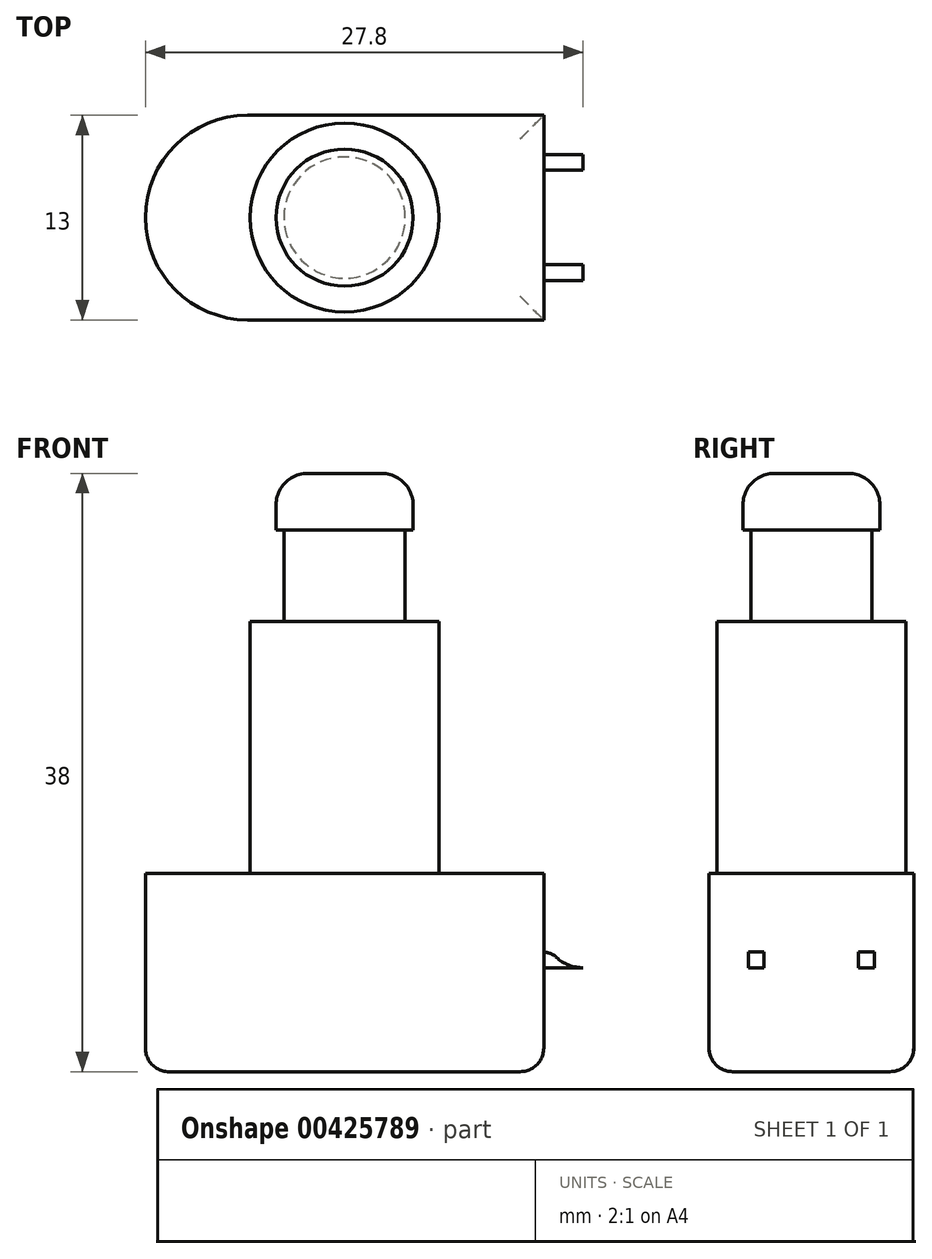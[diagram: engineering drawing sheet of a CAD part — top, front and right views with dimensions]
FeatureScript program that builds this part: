
annotation { "Feature Type Name" : "Feature", "Feature Type Description" : "" }
export const myFeature = defineFeature(function(context is Context, id is Id, definition is map)
    precondition{}
    {
        {
            var Q0;
            Q0=qCreatedBy(makeId("Top.planeOp"),FACE);
            var sketch = newSketch(context, id + "F0", { "sketchPlane" : qUnion([Q0])});
            skLineSegment(sketch, "E0.bottom", {"start": v(12.65, -6.5) * mm, "end": v(-6.15, -6.5) * mm});
            skLineSegment(sketch, "E0.top", {"start": v(12.65, 6.5) * mm, "end": v(-6.15, 6.5) * mm});
            skLineSegment(sketch, "E0.left", {"start": v(12.65, -6.5) * mm, "end": v(12.65, 6.5) * mm});
            skLineSegment(sketch, "E0.right", {"start": v(-12.65, 0) * mm, "end": v(-12.65, 0) * mm});
            skPoint(sketch, "E0.middle", {"position": v(0, 0) * mm});
            skPoint(sketch, "E1.visualSharp", {"position": v(-12.65, 6.5) * mm});
            skArc(sketch, "E1.filletArc", {"start": v(-6.15, 6.5) * mm, "mid": v(-10.75, 4.6) * mm, "end": v(-12.65, 0) * mm});
            skPoint(sketch, "E2.visualSharp", {"position": v(-12.65, -6.5) * mm});
            skArc(sketch, "E2.filletArc", {"start": v(-12.65, 0) * mm, "mid": v(-10.75, -4.6) * mm, "end": v(-6.15, -6.5) * mm});
            skSolve(sketch);
        }
        {
            var Q0;
            Q0 = qSketchRegion(id + "F0", true);
            extrude(context, id + "F1", {"entities" : qUnion([Q0]), "oppositeDirection" : true, "depth" : 12.6 * mm});
        }
        {
            var Q0;
            Q0=qCreatedBy(makeId("Top.planeOp"),FACE);
            var sketch = newSketch(context, id + "F2", { "sketchPlane" : qUnion([Q0])});
            skCircle(sketch, "E3", {"center": v(0, 0) * mm, "radius": 6 * mm});
            skSolve(sketch);
        }
        {
            var Q0;
            Q0 = qSketchRegion(id + "F2", true);
            extrude(context, id + "F3", {"entities" : qUnion([Q0]), "operationType" : NewBodyOperationType.ADD, "depth" : 16 * mm});
        }
        {
            var Q0;
            Q0=makeQuery(id+"F3.opExtrude","CAP_FACE",FACE,{"disambiguationData":[OSD([sQuery(id+"F2.wireOp",EDGE,"E3")])],"isStart":false});
            var sketch = newSketch(context, id + "F4", { "sketchPlane" : qUnion([Q0])});
            skCircle(sketch, "E4", {"center": v(0, 0) * mm, "radius": 3.85 * mm});
            skSolve(sketch);
        }
        {
            var Q0;
            Q0 = qSketchRegion(id + "F4", true);
            extrude(context, id + "F5", {"entities" : qUnion([Q0]), "operationType" : NewBodyOperationType.ADD, "depth" : (9.4 - 3.6) * mm});
        }
        {
            var Q0;
            Q0=makeQuery(id+"F5.opExtrude","CAP_FACE",FACE,{"disambiguationData":[OSD([sQuery(id+"F4.wireOp",EDGE,"E4")])],"isStart":false});
            var sketch = newSketch(context, id + "F6", { "sketchPlane" : qUnion([Q0])});
            skCircle(sketch, "E5", {"center": v(0, 0) * mm, "radius": 4.35 * mm});
            skSolve(sketch);
        }
        {
            var Q0;
            Q0 = qSketchRegion(id + "F6", true);
            extrude(context, id + "F7", {"entities" : qUnion([Q0]), "operationType" : NewBodyOperationType.ADD, "depth" : 3.6 * mm});
        }
        {
            var Q0;
            Q0=makeQuery(id+"F7.opExtrude","CAP_FACE",FACE,{"disambiguationData":[OSD([sQuery(id+"F6.wireOp",EDGE,"E5")])],"isStart":false});
            fillet(context, id + "F8", {"entities" : qUnion([Q0]), "radius" : 2 * mm, "tangentPropagation" : true, "allowEdgeOverflow" : false});
        }
        {
            var Q0;
            Q0=makeQuery(id+"F1.opExtrude","CAP_FACE",FACE,{"disambiguationData":[OSD([sQuery(id+"F0.wireOp",EDGE,"E0.bottom"),sQuery(id+"F0.wireOp",EDGE,"E0.top"),sQuery(id+"F0.wireOp",EDGE,"E0.left"),sQuery(id+"F0.wireOp",EDGE,"E1.filletArc"),sQuery(id+"F0.wireOp",EDGE,"E2.filletArc")])],"isStart":false});
            fillet(context, id + "F9", {"entities" : qUnion([Q0]), "radius" : 1.5 * mm, "tangentPropagation" : true, "allowEdgeOverflow" : false});
        }
        {
            var Q0;
            Q0=makeQuery(id+"F1.opExtrude","SWEPT_FACE",FACE,{"disambiguationData":[OSD([sQuery(id+"F0.wireOp",EDGE,"E0.left")])]});
            var sketch = newSketch(context, id + "F10", { "sketchPlane" : qUnion([Q0])});
            skLineSegment(sketch, "E6.bottom", {"start": v(-4, -1) * mm, "end": v(-3, -1) * mm});
            skLineSegment(sketch, "E6.top", {"start": v(-4, -6) * mm, "end": v(-3, -6) * mm});
            skLineSegment(sketch, "E6.left", {"start": v(-4, -1) * mm, "end": v(-4, -6) * mm});
            skLineSegment(sketch, "E6.right", {"start": v(-3, -1) * mm, "end": v(-3, -6) * mm});
            skLineSegment(sketch, "E7", {"start": v(0, 0) * mm, "end": v(0, -15.59) * mm, "construction": true});
            skLineSegment(sketch, "E8.MirrorCS", {"start": v(4, -1) * mm, "end": v(4, -6) * mm});
            skLineSegment(sketch, "E9.MirrorCS", {"start": v(4, -6) * mm, "end": v(3, -6) * mm});
            skLineSegment(sketch, "E10.MirrorCS", {"start": v(4, -1) * mm, "end": v(3, -1) * mm});
            skLineSegment(sketch, "E11.MirrorCS", {"start": v(3, -1) * mm, "end": v(3, -6) * mm});
            skSolve(sketch);
        }
        {
            var Q0;
            Q0 = qSketchRegion(id + "F10", true);
            extrude(context, id + "F11", {"entities" : qUnion([Q0]), "operationType" : NewBodyOperationType.ADD, "depth" : 5 * mm});
        }
        {
            var Q0;
            Q0=makeQuery(id+"F11.opExtrude","SWEPT_FACE",FACE,{"disambiguationData":[OSD([sQuery(id+"F10.wireOp",EDGE,"E6.left")])]});
            var sketch = newSketch(context, id + "F12", { "sketchPlane" : qUnion([Q0])});
            skCircle(sketch, "E12", {"center": v(15.15, -3.5) * mm, "radius": 1.2 * mm});
            skPoint(sketch, "E12.centerSnap0", {"position": v(15.15, -1) * mm});
            skPoint(sketch, "E12.centerSnap1", {"position": v(17.65, -3.5) * mm});
            skArc(sketch, "E13", {"start": v(13.45, -5.33) * mm, "mid": v(17.65, -3.5) * mm, "end": v(13.45, -1.67) * mm});
            skArc(sketch, "E14", {"start": v(12.65, -2) * mm, "mid": v(13.08, -1.9) * mm, "end": v(13.45, -1.67) * mm});
            skLineSegment(sketch, "E15", {"start": v(15.15, -3.5) * mm, "end": v(10.86, -3.5) * mm, "construction": true});
            skArc(sketch, "E16.MirrorCS", {"start": v(12.65, -5) * mm, "mid": v(13.08, -5.1) * mm, "end": v(13.45, -5.33) * mm});
            skSolve(sketch);
        }
        {
            var Q0;
            Q0 = qSketchRegion(id + "F12", true);
            var Q1;
            {var subQ0=sQuery(id+"F12.wireOp",EDGE,"E14");Q1=makeQuery(id+"F12.imprint","IMPRINT",FACE,{"disambiguationData":[TD([[makeQuery(id+"F12.imprint","IMPRINT",EDGE,{"derivedFrom":subQ0}),1.0]])]});}
            var Q2;
            {var subQ0=sQuery(id+"F12.wireOp",EDGE,"E13");var subQ1=sQuery(id+"F10.wireOp",EDGE,"E6.left");var subQ2=makeQuery(id+"F11.opExtrude","CAP_EDGE",EDGE,{"disambiguationData":[OSD([subQ1])],"isStart":false});var subQ3=makeQuery(id+"F12.imprint","INTERSECT",VERTEX,{"derivedFrom":[subQ2,subQ0]});Q2=makeQuery(id+"F12.imprint","IMPRINT",FACE,{"disambiguationData":[TD([[makeQuery(id+"F12.imprint","IMPRINT",EDGE,{"disambiguationData":[TD([[subQ3,-1.0]])],"derivedFrom":subQ0}),-1.0]])]});}
            var Q3;
            {var subQ0=sQuery(id+"F12.wireOp",EDGE,"E13");var subQ1=sQuery(id+"F10.wireOp",EDGE,"E6.left");var subQ4=makeQuery(id+"F11.opExtrude","CAP_EDGE",EDGE,{"disambiguationData":[OSD([subQ1])],"isStart":false});var subQ5=makeQuery(id+"F12.imprint","INTERSECT",VERTEX,{"derivedFrom":[subQ4,subQ0]});Q3=makeQuery(id+"F12.imprint","IMPRINT",FACE,{"disambiguationData":[TD([[makeQuery(id+"F12.imprint","IMPRINT",EDGE,{"disambiguationData":[TD([[subQ5,1.0]])],"derivedFrom":subQ0}),-1.0]])]});}
            var Q4;
            {var subQ0=sQuery(id+"F12.wireOp",EDGE,"E16.MirrorCS");Q4=makeQuery(id+"F12.imprint","IMPRINT",FACE,{"disambiguationData":[TD([[makeQuery(id+"F12.imprint","IMPRINT",EDGE,{"derivedFrom":subQ0}),-1.0]])]});}
            extrude(context, id + "F13", {"entities" : qUnion([Q0, Q1, Q2, Q3, Q4]), "operationType" : NewBodyOperationType.REMOVE, "endBound" : BoundingType.THROUGH_ALL, "oppositeDirection" : true, "depth" : 25 * mm});
        }
    });
